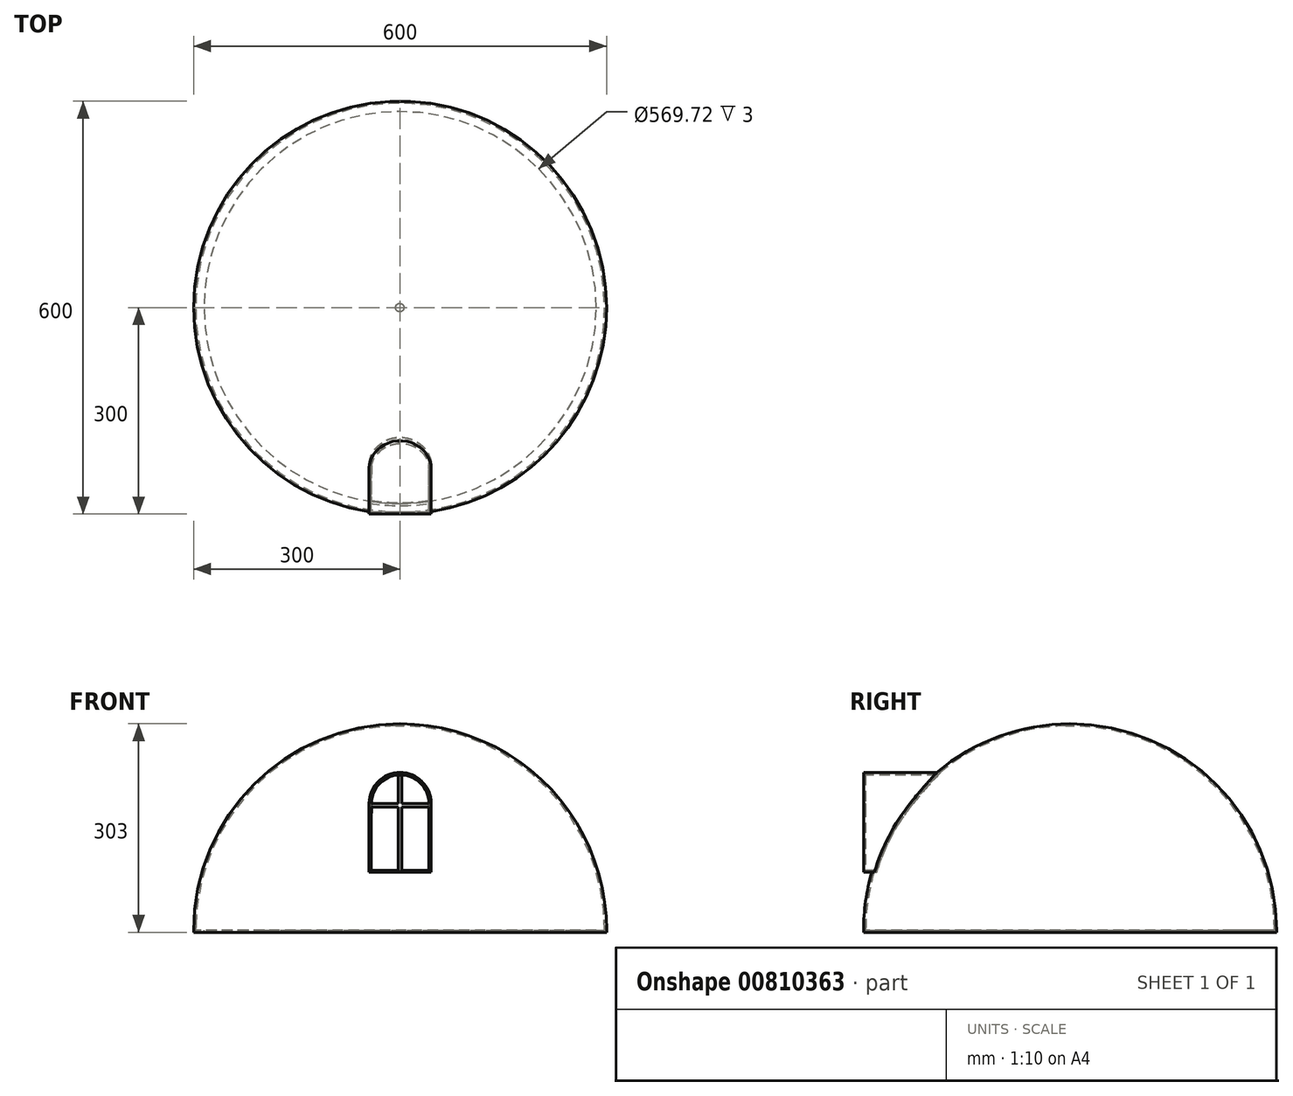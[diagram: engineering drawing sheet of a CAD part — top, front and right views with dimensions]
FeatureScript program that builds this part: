
annotation { "Feature Type Name" : "Feature", "Feature Type Description" : "" }
export const myFeature = defineFeature(function(context is Context, id is Id, definition is map)
    precondition{}
    {
        {
            var Q0;
            Q0=qCreatedBy(makeId("Front.planeOp"),FACE);
            var sketch = newSketch(context, id + "F0", { "sketchPlane" : qUnion([Q0])});
            skLineSegment(sketch, "E0", {"start": v(0, 0) * mm, "end": v(15.14, 0) * mm});
            skArc(sketch, "E1", {"start": v(300, 300) * mm, "mid": v(87.87, 212.13) * mm, "end": v(0, 0) * mm});
            skArc(sketch, "E2.0", {"start": v(596.97, -4) * mm, "mid": v(597, -2) * mm, "end": v(597, 0) * mm});
            skLineSegment(sketch, "E3", {"start": v(300, 300) * mm, "end": v(300, 0) * mm});
            skLineSegment(sketch, "E4", {"start": v(0, 0) * mm, "end": v(0, -3) * mm});
            skLineSegment(sketch, "E5", {"start": v(0, -3) * mm, "end": v(15.14, -3) * mm});
            skLineSegment(sketch, "E6", {"start": v(15.14, -3) * mm, "end": v(15.14, 0) * mm});
            skPoint(sketch, "E7.orphan", {"position": v(300, 383.48) * mm});
            skArc(sketch, "E8.trimOffspring", {"start": v(300, 297) * mm, "mid": v(88.58, 208.6) * mm, "end": v(3.03, -4) * mm});
            skLineSegment(sketch, "E9.trimOffspring", {"start": v(597, 0) * mm, "end": v(600, 0) * mm});
            skSolve(sketch);
        }
        {
            var Q0;
            Q0 = qSketchRegion(id + "F0", true);
            var Q1;
            Q1=sQuery(id+"F0.wireOp",EDGE,"E3");
            revolve(context, id + "F1", {"surfaceOperationType" : NewSurfaceOperationType.NEW, "entities" : qUnion([Q0]), "axis" : qUnion([Q1]), "revolveType" : RevolveType.FULL});
        }
        {
            var Q0;
            Q0=qCreatedBy(makeId("Front.planeOp"),FACE);
            var sketch = newSketch(context, id + "F2", { "sketchPlane" : qUnion([Q0])});
            skLineSegment(sketch, "E10.top", {"start": v(255, 84.24) * mm, "end": v(345, 84.24) * mm});
            skLineSegment(sketch, "E10.left", {"start": v(255, 184.24) * mm, "end": v(255, 84.24) * mm});
            skLineSegment(sketch, "E10.right", {"start": v(345, 184.24) * mm, "end": v(345, 84.24) * mm});
            skArc(sketch, "E11", {"start": v(345, 184.24) * mm, "mid": v(300, 229.24) * mm, "end": v(255, 184.24) * mm});
            skLineSegment(sketch, "E12.0", {"start": v(258, 184.24) * mm, "end": v(258, 87.24) * mm});
            skArc(sketch, "E12.1", {"start": v(342, 184.24) * mm, "mid": v(300, 226.24) * mm, "end": v(258, 184.24) * mm});
            skLineSegment(sketch, "E12.2", {"start": v(342, 184.24) * mm, "end": v(342, 87.24) * mm});
            skLineSegment(sketch, "E12.3", {"start": v(258, 87.24) * mm, "end": v(342, 87.24) * mm});
            skSolve(sketch);
        }
        {
            var Q0;
            Q0 = qSketchRegion(id + "F2", true);
            extrude(context, id + "F3", {"entities" : qUnion([Q0]), "operationType" : NewBodyOperationType.ADD, "depth" : 300 * mm, "offsetDistance" : 25 * mm});
        }
        {
            var Q0;
            Q0=qCreatedBy(makeId("Front.planeOp"),FACE);
            var sketch = newSketch(context, id + "F4", { "sketchPlane" : qUnion([Q0])});
            skLineSegment(sketch, "E13", {"start": v(257.99, 87.24) * mm, "end": v(342, 87.24) * mm});
            skLineSegment(sketch, "E14", {"start": v(342, 87.24) * mm, "end": v(342, 184.08) * mm});
            skLineSegment(sketch, "E15", {"start": v(342, 184.08) * mm, "end": v(258.33, 184.08) * mm});
            skLineSegment(sketch, "E16", {"start": v(258.33, 184.08) * mm, "end": v(257.99, 87.24) * mm});
            skLineSegment(sketch, "E17", {"start": v(257.99, 87.24) * mm, "end": v(258.33, 184.08) * mm});
            skArc(sketch, "E18", {"start": v(342, 184.08) * mm, "mid": v(300.16, 225.77) * mm, "end": v(258.33, 184.08) * mm});
            skSolve(sketch);
        }
        {
            var Q0;
            Q0 = qSketchRegion(id + "F4", true);
            extrude(context, id + "F5", {"entities" : qUnion([Q0]), "operationType" : NewBodyOperationType.REMOVE, "depth" : 350 * mm, "offsetDistance" : 25 * mm});
        }
        {
            var Q0;
            Q0=qCreatedBy(makeId("Front.planeOp"),FACE);
            var sketch = newSketch(context, id + "F6", { "sketchPlane" : qUnion([Q0])});
            skLineSegment(sketch, "E19", {"start": v(299.9, 297.03) * mm, "end": v(299.9, 0) * mm});
            skLineSegment(sketch, "E20", {"start": v(299.9, 0) * mm, "end": v(2.97, 0) * mm});
            skArc(sketch, "E21", {"start": v(299.9, 297.03) * mm, "mid": v(90.3, 209.62) * mm, "end": v(2.97, 0) * mm});
            skSolve(sketch);
        }
        {
            var Q0;
            Q0 = qSketchRegion(id + "F6", true);
            var Q1;
            Q1=sQuery(id+"F6.wireOp",EDGE,"E19");
            revolve(context, id + "F7", {"operationType" : NewBodyOperationType.REMOVE, "surfaceOperationType" : NewSurfaceOperationType.NEW, "entities" : qUnion([Q0]), "axis" : qUnion([Q1]), "revolveType" : RevolveType.FULL, "oppositeDirection" : true});
        }
        {
            var Q0;
            Q0=makeQuery(id+"F3.opExtrude","CAP_FACE",FACE,{"disambiguationData":[OSD([sQuery(id+"F2.wireOp",EDGE,"E10.top"),sQuery(id+"F2.wireOp",EDGE,"E10.left"),sQuery(id+"F2.wireOp",EDGE,"E10.right"),sQuery(id+"F2.wireOp",EDGE,"E11"),sQuery(id+"F2.wireOp",EDGE,"E12.0"),sQuery(id+"F2.wireOp",EDGE,"E12.1"),sQuery(id+"F2.wireOp",EDGE,"E12.2"),sQuery(id+"F2.wireOp",EDGE,"E12.3")])],"isStart":false});
            var sketch = newSketch(context, id + "F8", { "sketchPlane" : qUnion([Q0])});
            skLineSegment(sketch, "E22", {"start": v(258, 184.24) * mm, "end": v(297.5, 184.24) * mm});
            skLineSegment(sketch, "E23.0", {"start": v(302.5, 225.55) * mm, "end": v(302.5, 184.24) * mm});
            skLineSegment(sketch, "E24.0", {"start": v(258, 179.24) * mm, "end": v(297.5, 179.24) * mm});
            skLineSegment(sketch, "E25.0", {"start": v(297.5, 225.55) * mm, "end": v(297.5, 184.24) * mm});
            skPoint(sketch, "E26.orphan", {"position": v(300, 226.24) * mm});
            skLineSegment(sketch, "E27.trimOffspring", {"start": v(302.5, 179.24) * mm, "end": v(302.5, 87.24) * mm});
            skLineSegment(sketch, "E28.trimOffspring", {"start": v(302.5, 184.24) * mm, "end": v(342, 184.24) * mm});
            skLineSegment(sketch, "E29.trimOffspring", {"start": v(297.5, 179.24) * mm, "end": v(297.5, 87.24) * mm});
            skLineSegment(sketch, "E30.trimOffspring", {"start": v(302.5, 179.24) * mm, "end": v(342, 179.24) * mm});
            skPoint(sketch, "E31.end.orphan", {"position": v(300, 87.24) * mm});
            skLineSegment(sketch, "E32", {"start": v(258, 184.24) * mm, "end": v(258, 179.24) * mm});
            skLineSegment(sketch, "E33", {"start": v(342, 184.24) * mm, "end": v(342, 179.24) * mm});
            skLineSegment(sketch, "E34", {"start": v(297.5, 225.55) * mm, "end": v(302.5, 225.55) * mm});
            skPoint(sketch, "E35.orphan", {"position": v(302.5, 226.24) * mm});
            skSolve(sketch);
        }
        {
            var Q0;
            Q0 = qSketchRegion(id + "F8", true);
            var Q1;
            Q1=makeQuery(id+"F8.imprint","IMPRINT",FACE,{"disambiguationData":[TD([[makeQuery(id+"F8.imprint","IMPRINT",EDGE,{"derivedFrom":sQuery(id+"F8.wireOp",EDGE,"E22")}),-1.0]])]});
            extrude(context, id + "F9", {"entities" : qUnion([Q0, Q1]), "operationType" : NewBodyOperationType.ADD, "oppositeDirection" : true, "depth" : 3 * mm, "offsetDistance" : 25 * mm});
        }
    });
